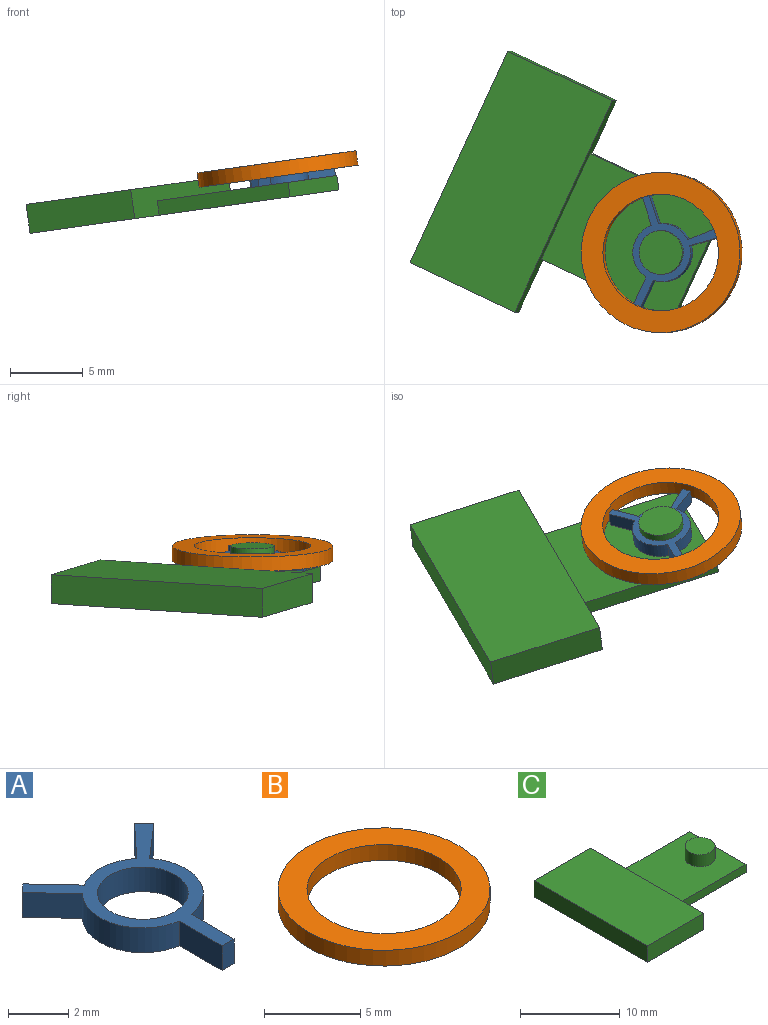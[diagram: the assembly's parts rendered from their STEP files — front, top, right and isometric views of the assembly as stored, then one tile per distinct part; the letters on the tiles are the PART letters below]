
ASSEMBLY  parts=3 mates=2
PART A: 15 faces, bbox 5.9x7.2x1 mm
  f0: cylinder r=2mm len=3.37mm, axis (0,0,-1), area 4.4mm2, adj f1,f12,f13,f14
  f1: plane 2.01x1mm, normal (-1,0,0), area 2mm2, adj f0,f2,f13,f14
  f2: plane 1x0.56mm, normal (0,-1,0), area 0.6mm2, adj f1,f3,f13,f14
  f3: plane 2.01x1mm, normal (1,0,0), area 2mm2, adj f2,f4,f13,f14
  f4: cylinder r=2mm len=3.23mm, axis (0,0,-1), area 4.2mm2, adj f3,f5,f13,f14
  f5: plane 1.51x1.31mm, normal (0.65,-0.76,0), area 2mm2, adj f4,f6,f13,f14
  f6: plane 1x0.46mm, normal (0.72,0.7,0), area 0.6mm2, adj f5,f7,f13,f14
  f7: plane 1.47x1.36mm, normal (-0.73,0.68,0), area 2mm2, adj f6,f8,f13,f14
  f8: cylinder r=2mm len=2.32mm, axis (0,0,-1), area 2.5mm2, adj f7,f9,f13,f14
  f9: plane 1.48x1.38mm, normal (0.73,0.68,0), area 2mm2, adj f8,f10,f13,f14
  f10: plane 1x0.37mm, normal (-0.65,0.76,0), area 0.5mm2, adj f9,f12,f13,f14
  f11: cylinder r=1.5mm len=3mm, axis (0,0,-1), area 9.4mm2, adj f13,f14
  f12: plane 1.47x1.36mm, normal (-0.73,-0.68,0), area 2mm2, adj f0,f10,f13,f14
  f13: plane 7.17x5.88mm, normal (0,0,1), area 8.7mm2, adj f0,f1,f2,f3,f4,f5,f6,f7
  f14: plane 7.17x5.88mm, normal (0,0,-1), area 8.7mm2, adj f0,f1,f2,f3,f4,f5,f6,f7
PART B: 4 faces, bbox 11x11x1 mm
  f0: cylinder r=4mm len=8mm, axis (0,0,-1), area 25.1mm2, adj f2,f3
  f1: cylinder r=5.5mm len=11mm, axis (0,0,-1), area 34.6mm2, adj f2,f3
  f2: plane 11x11mm, normal (0,0,1), area 44.8mm2, adj f0,f1
  f3: plane 11x11mm, normal (0,0,-1), area 44.8mm2, adj f0,f1
PART C: 12 faces, bbox 18x16x2.5 mm
  f0: plane 16x2mm, normal (1,0,0), area 24mm2, adj f1,f3,f4,f5,f6,f7,f9
  f1: plane 8x2mm, normal (0,1,0), area 16mm2, adj f0,f2,f4,f5
  f2: plane 16x2mm, normal (-1,0,0), area 32mm2, adj f1,f3,f4,f5
  f3: plane 8x2mm, normal (0,-1,0), area 16mm2, adj f0,f2,f4,f5
  f4: plane 16x8mm, normal (0,0,1), area 128mm2, adj f0,f1,f2,f3
  f5: plane 18x16mm, normal (0,0,-1), area 208mm2, adj f0,f1,f2,f3,f6,f7,f8
  f6: plane 10x1mm, normal (0,1,0), area 10mm2, adj f0,f5,f8,f9
  f7: plane 10x1mm, normal (0,-1,0), area 10mm2, adj f0,f5,f8,f9
  f8: plane 8x1mm, normal (1,0,0), area 8mm2, adj f5,f6,f7,f9
  f9: plane 10x8mm, normal (0,0,1), area 72.9mm2, adj f0,f6,f7,f8,f11
  f10: plane 3x3mm, normal (0,0,1), area 7.1mm2, adj f11
  f11: cylinder r=1.5mm len=3mm, axis (0,0,-1), area 14.1mm2, adj f9,f10
PLACE A rot(axis=(0.07,-0.3,-0.95),26.2deg) t=(-25.52,-19.69,-3.88)mm
PLACE B rot(axis=(0.07,-0.3,-0.95),26.2deg) t=(-25.59,-19.69,-3.38)mm
PLACE C rot(axis=(0.07,-0.3,-0.95),26.2deg) t=(19.22,-6.5,1.39)mm
MATE fastened A.f11 <-> C.f11  axis (0.14,0,-0.99) through (-25.52,-19.69,-3.88)mm
MATE fastened B.f0 <-> C.f11  axis (-0.14,0,0.99) through (-25.73,-19.69,-2.39)mm
